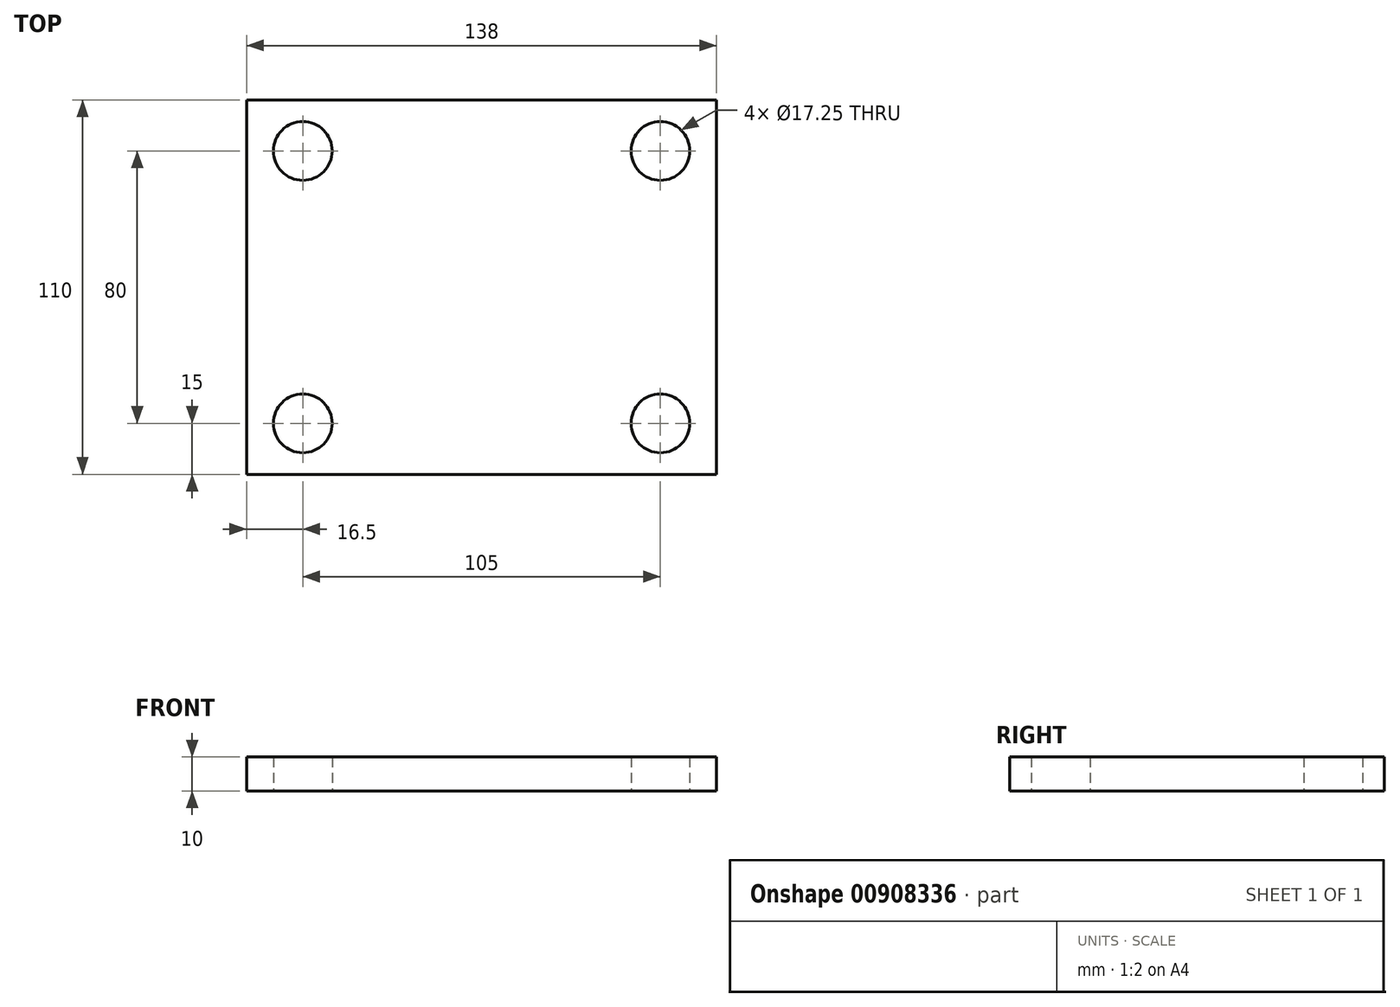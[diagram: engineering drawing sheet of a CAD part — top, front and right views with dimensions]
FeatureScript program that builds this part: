
annotation { "Feature Type Name" : "Feature", "Feature Type Description" : "" }
export const myFeature = defineFeature(function(context is Context, id is Id, definition is map)
    precondition{}
    {
        {
            var Q0;
            Q0=qCreatedBy(makeId("Top.planeOp"),FACE);
            var sketch = newSketch(context, id + "F0", { "sketchPlane" : qUnion([Q0])});
            skLineSegment(sketch, "E0.bottom", {"start": v(69, 55) * mm, "end": v(-69, 55) * mm});
            skLineSegment(sketch, "E0.top", {"start": v(69, -55) * mm, "end": v(-69, -55) * mm});
            skLineSegment(sketch, "E0.left", {"start": v(69, 55) * mm, "end": v(69, -55) * mm});
            skLineSegment(sketch, "E0.right", {"start": v(-69, 55) * mm, "end": v(-69, -55) * mm});
            skPoint(sketch, "E0.middle", {"position": v(0, 0) * mm});
            skCircle(sketch, "E1", {"center": v(-52.5, 40) * mm, "radius": 5 * mm});
            skCircle(sketch, "E2", {"center": v(-52.5, -40) * mm, "radius": 5 * mm});
            skCircle(sketch, "E3", {"center": v(52.5, 40) * mm, "radius": 5 * mm});
            skCircle(sketch, "E4", {"center": v(52.5, -40) * mm, "radius": 5 * mm});
            skSolve(sketch);
        }
        {
            var Q0;
            Q0=makeQuery(id+"F0.imprint","IMPRINT",FACE,{"disambiguationData":[TD([[makeQuery(id+"F0.imprint","IMPRINT",EDGE,{"derivedFrom":sQuery(id+"F0.wireOp",EDGE,"E4")}),1.0]])]});
            var Q1;
            Q1=makeQuery(id+"F0.imprint","IMPRINT",FACE,{"disambiguationData":[TD([[makeQuery(id+"F0.imprint","IMPRINT",EDGE,{"derivedFrom":sQuery(id+"F0.wireOp",EDGE,"E0.bottom")}),1.0]])]});
            var Q2;
            Q2=makeQuery(id+"F0.imprint","IMPRINT",FACE,{"disambiguationData":[TD([[makeQuery(id+"F0.imprint","IMPRINT",EDGE,{"derivedFrom":sQuery(id+"F0.wireOp",EDGE,"E1")}),1.0]])]});
            var Q3;
            Q3=makeQuery(id+"F0.imprint","IMPRINT",FACE,{"disambiguationData":[TD([[makeQuery(id+"F0.imprint","IMPRINT",EDGE,{"derivedFrom":sQuery(id+"F0.wireOp",EDGE,"E2")}),1.0]])]});
            var Q4;
            Q4=makeQuery(id+"F0.imprint","IMPRINT",FACE,{"disambiguationData":[TD([[makeQuery(id+"F0.imprint","IMPRINT",EDGE,{"derivedFrom":sQuery(id+"F0.wireOp",EDGE,"E3")}),1.0]])]});
            extrude(context, id + "F1", {"entities" : qUnion([Q0, Q1, Q2, Q3, Q4]), "depth" : 10 * mm, "offsetDistance" : 25 * mm});
        }
        {
            var Q0;
            Q0=sQuery(id+"F0.wireOp",VERTEX,"E1.center");
            var Q1;
            Q1=sQuery(id+"F0.wireOp",VERTEX,"E3.center");
            var Q2;
            Q2=sQuery(id+"F0.wireOp",VERTEX,"E2.center");
            var Q3;
            Q3=sQuery(id+"F0.wireOp",VERTEX,"E4.center");
            var Q4;
            Q4=makeQuery(id+"F1.opExtrude","SWEPT_BODY",BODY,{"disambiguationData":[OSD([sQuery(id+"F0.wireOp",EDGE,"E0.bottom"),sQuery(id+"F0.wireOp",EDGE,"E0.top"),sQuery(id+"F0.wireOp",EDGE,"E0.left"),sQuery(id+"F0.wireOp",EDGE,"E0.right")])]});
            hole(context, id + "F2", {"style" : HoleStyle.C_BORE, "endStyle" : HoleEndStyle.THROUGH, "oppositeDirection" : true, "standardTappedOrClearance" : lookupTablePath({ "fit" : "Normal", "standard" : "ISO", "size" : "M10", "type" : "Clearance" }), "standardBlindInLast" : lookupTablePath({ "fit" : "Normal", "standard" : "ISO", "size" : "M10", "type" : "Clearance" }), "holeDiameter" : 11 * mm, "cBoreDiameter" : 17.25 * mm, "cBoreDepth" : 10 * mm, "majorDiameter" : 5 * mm, "isTappedThrough" : true, "tappedDepth" : 12 * mm, "tapClearance" : 3, "locations" : qUnion([Q0, Q1, Q2, Q3]), "scope" : qUnion([Q4])});
        }
    });
